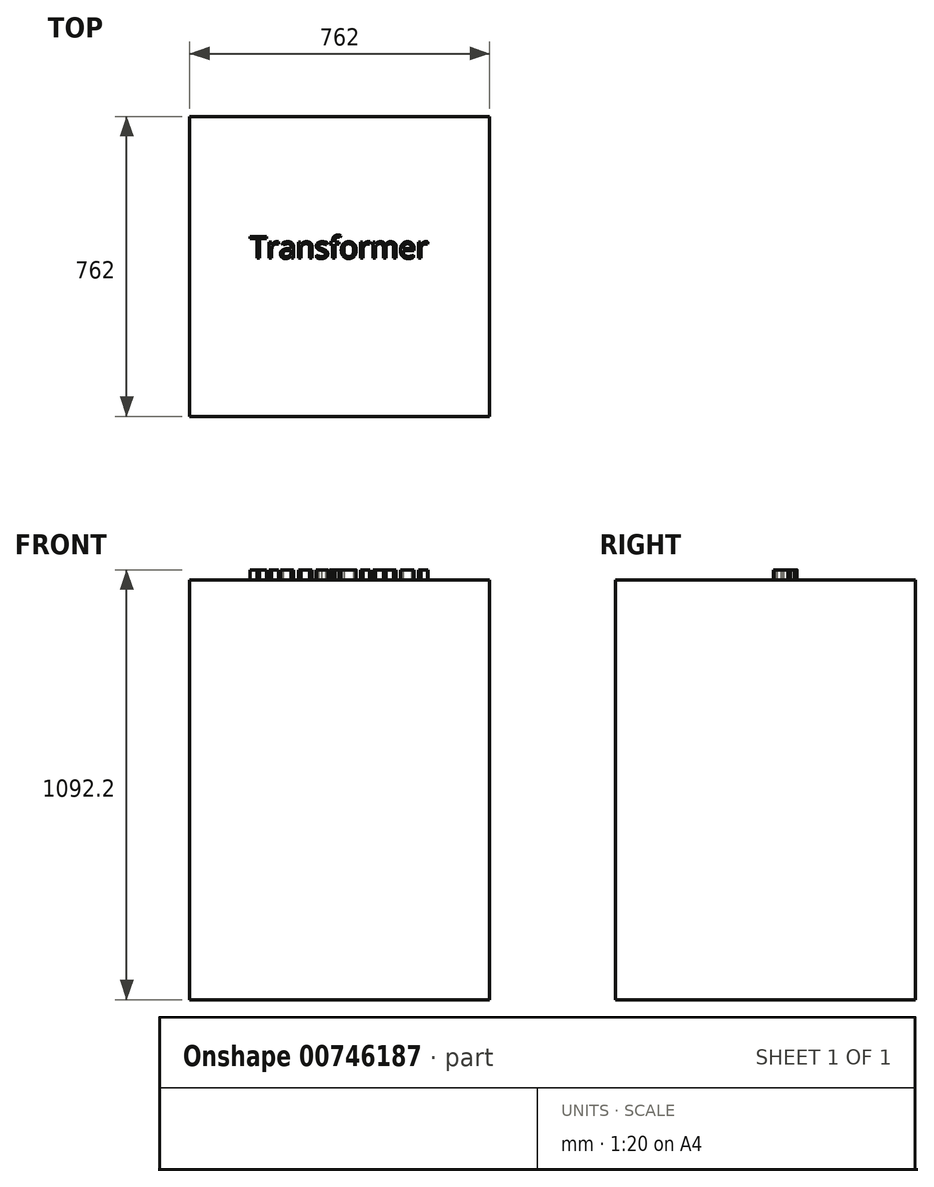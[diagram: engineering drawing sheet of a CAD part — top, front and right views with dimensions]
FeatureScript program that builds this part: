
annotation { "Feature Type Name" : "Feature", "Feature Type Description" : "" }
export const myFeature = defineFeature(function(context is Context, id is Id, definition is map)
    precondition{}
    {
        {
            var Q0;
            Q0=qCreatedBy(makeId("Top.planeOp"),FACE);
            var sketch = newSketch(context, id + "F0", { "sketchPlane" : qUnion([Q0])});
            skLineSegment(sketch, "E0.bottom", {"start": v(381, -381) * mm, "end": v(-381, -381) * mm});
            skLineSegment(sketch, "E0.top", {"start": v(381, 381) * mm, "end": v(-381, 381) * mm});
            skLineSegment(sketch, "E0.left", {"start": v(381, -381) * mm, "end": v(381, 381) * mm});
            skLineSegment(sketch, "E0.right", {"start": v(-381, -381) * mm, "end": v(-381, 381) * mm});
            skPoint(sketch, "E0.middle", {"position": v(0, 0) * mm});
            skSolve(sketch);
        }
        {
            var Q0;
            Q0 = qSketchRegion(id + "F0", true);
            extrude(context, id + "F1", {"entities" : qUnion([Q0]), "depth" : 1066.8 * mm, "offsetDistance" : 30.48 * mm});
        }
        {
            var Q0;
            Q0=makeQuery(id+"F1.opExtrude","CAP_FACE",FACE,{"disambiguationData":[OSD([sQuery(id+"F0.wireOp",EDGE,"E0.bottom"),sQuery(id+"F0.wireOp",EDGE,"E0.top"),sQuery(id+"F0.wireOp",EDGE,"E0.left"),sQuery(id+"F0.wireOp",EDGE,"E0.right")])],"isStart":false});
            var sketch = newSketch(context, id + "F2", { "sketchPlane" : qUnion([Q0])});
            skText(sketch, "E1", { "text": "Transformer\n", "fontName": "OpenSans-Regular.ttf"});
            const initialGuessF2  = {"E1": [-0.2286, 0.0205, 1, 0, 0.0557]};
            skSetInitialGuess(sketch, initialGuessF2);
            skSolve(sketch);
        }
        {
            var Q0;
            Q0 = qSketchRegion(id + "F2", true);
            extrude(context, id + "F3", {"entities" : qUnion([Q0]), "operationType" : NewBodyOperationType.ADD, "depth" : 25.4 * mm, "offsetDistance" : 30.48 * mm});
        }
    });
